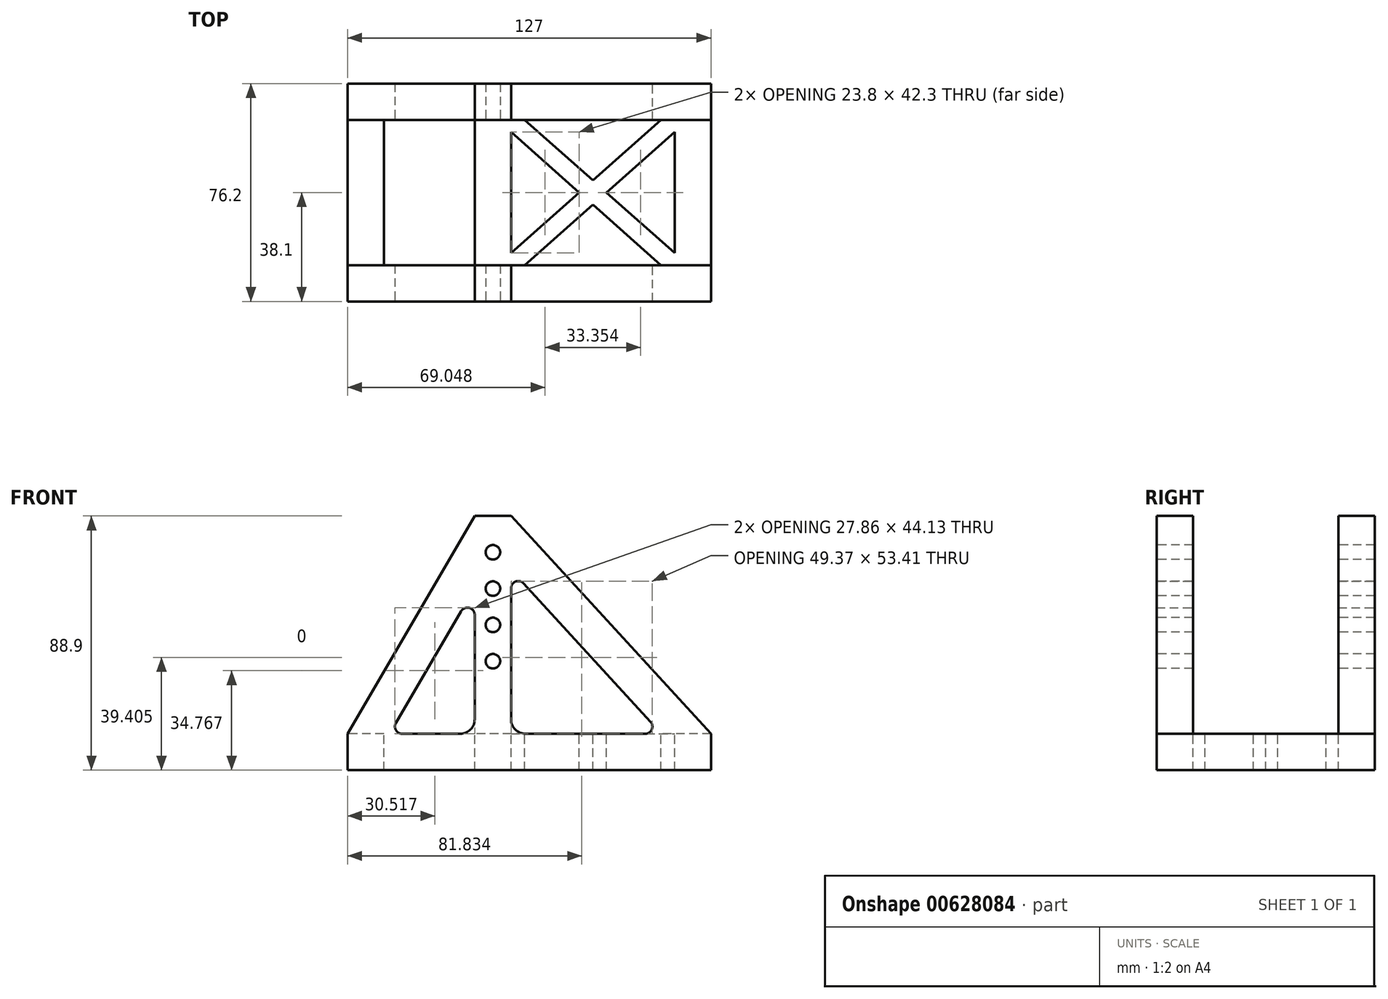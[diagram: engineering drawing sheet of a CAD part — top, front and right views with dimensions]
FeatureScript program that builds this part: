
annotation { "Feature Type Name" : "Feature", "Feature Type Description" : "" }
export const myFeature = defineFeature(function(context is Context, id is Id, definition is map)
    precondition{}
    {
        {
            var Q0;
            Q0=qCreatedBy(makeId("Front.planeOp"),FACE);
            var sketch = newSketch(context, id + "F0", { "sketchPlane" : qUnion([Q0])});
            skLineSegment(sketch, "E0", {"start": v(0, 0) * mm, "end": v(76.2, 0) * mm});
            skLineSegment(sketch, "E1", {"start": v(76.2, 0) * mm, "end": v(-50.8, 0) * mm});
            skLineSegment(sketch, "E2", {"start": v(-50.8, 0) * mm, "end": v(-50.8, 12.7) * mm});
            skLineSegment(sketch, "E3", {"start": v(-36.1, 12.7) * mm, "end": v(-6.35, 12.7) * mm});
            skLineSegment(sketch, "E4", {"start": v(76.2, 12.7) * mm, "end": v(76.2, 0) * mm});
            skLineSegment(sketch, "E5", {"start": v(0, 0) * mm, "end": v(0, 88.9) * mm, "construction": true});
            skLineSegment(sketch, "E6.bottom", {"start": v(6.35, 88.9) * mm, "end": v(-6.35, 88.9) * mm});
            skLineSegment(sketch, "E6.top", {"start": v(6.35, 88.9) * mm, "end": v(-6.35, 88.9) * mm});
            skLineSegment(sketch, "E6.left", {"start": v(6.35, 88.9) * mm, "end": v(6.35, 88.9) * mm});
            skLineSegment(sketch, "E6.right", {"start": v(-6.35, 88.9) * mm, "end": v(-6.35, 88.9) * mm});
            skPoint(sketch, "E6.middle", {"position": v(0, 88.9) * mm});
            skLineSegment(sketch, "E7", {"start": v(-6.35, 88.9) * mm, "end": v(-50.8, 12.7) * mm});
            skLineSegment(sketch, "E8", {"start": v(6.35, 88.9) * mm, "end": v(76.2, 12.7) * mm});
            skLineSegment(sketch, "E9", {"start": v(-6.35, 63.7) * mm, "end": v(-6.35, 12.7) * mm});
            skLineSegment(sketch, "E10.trimOffspring", {"start": v(-6.35, 63.7) * mm, "end": v(-36.1, 12.7) * mm});
            skLineSegment(sketch, "E11.trimOffspring", {"start": v(6.35, 70.1) * mm, "end": v(58.97, 12.7) * mm});
            skLineSegment(sketch, "E12.trimOffspring", {"start": v(6.35, 70.1) * mm, "end": v(6.35, 12.7) * mm});
            skLineSegment(sketch, "E13.trimOffspring", {"start": v(6.35, 12.7) * mm, "end": v(58.97, 12.7) * mm});
            skPoint(sketch, "E14.orphan", {"position": v(6.35, 0) * mm});
            skPoint(sketch, "E15", {"position": v(0, 76.2) * mm});
            skPoint(sketch, "E16", {"position": v(0, 63.5) * mm});
            skPoint(sketch, "E17", {"position": v(0, 50.8) * mm});
            skPoint(sketch, "E18", {"position": v(0, 38.1) * mm});
            skCircle(sketch, "E19", {"center": v(0, 38.1) * mm, "radius": 2.25 * mm});
            skCircle(sketch, "E20", {"center": v(0, 50.8) * mm, "radius": 2.25 * mm});
            skCircle(sketch, "E21", {"center": v(0, 63.5) * mm, "radius": 2.25 * mm});
            skCircle(sketch, "E22", {"center": v(0, 76.2) * mm, "radius": 2.25 * mm});
            skSolve(sketch);
        }
        {
            var Q0;
            Q0 = qSketchRegion(id + "F0", true);
            extrude(context, id + "F1", {"entities" : qUnion([Q0]), "depth" : 76.2 * mm, "offsetDistance" : 25.4 * mm});
        }
        {
            var Q0;
            Q0=makeQuery(id+"F1.opExtrude","SWEPT_FACE",FACE,{"disambiguationData":[OSD([sQuery(id+"F0.wireOp",EDGE,"E2")])]});
            var sketch = newSketch(context, id + "F2", { "sketchPlane" : qUnion([Q0])});
            skLineSegment(sketch, "E23.bottom", {"start": v(0, 0) * mm, "end": v(76.2, 0) * mm});
            skLineSegment(sketch, "E23.top", {"start": v(0, 12.7) * mm, "end": v(76.2, 12.7) * mm});
            skLineSegment(sketch, "E23.left", {"start": v(0, 0) * mm, "end": v(0, 12.7) * mm});
            skLineSegment(sketch, "E23.right", {"start": v(76.2, 0) * mm, "end": v(76.2, 12.7) * mm});
            skLineSegment(sketch, "E24", {"start": v(76.2, 12.7) * mm, "end": v(63.5, 12.7) * mm});
            skLineSegment(sketch, "E25", {"start": v(12.7, 12.7) * mm, "end": v(12.7, 88.9) * mm});
            skLineSegment(sketch, "E26", {"start": v(12.7, 88.9) * mm, "end": v(63.5, 88.9) * mm});
            skLineSegment(sketch, "E27", {"start": v(63.5, 88.9) * mm, "end": v(63.5, 12.7) * mm});
            skSolve(sketch);
        }
        {
            var Q0;
            {var subQ2=sQuery(id+"F2.wireOp",EDGE,"E25");Q0=makeQuery(id+"F2.imprint","IMPRINT",FACE,{"disambiguationData":[TD([[makeQuery(id+"F2.imprint","IMPRINT",EDGE,{"derivedFrom":subQ2}),-1.0]])]});}
            extrude(context, id + "F3", {"entities" : qUnion([Q0]), "operationType" : NewBodyOperationType.REMOVE, "oppositeDirection" : true, "depth" : 254 * mm, "offsetDistance" : 25.4 * mm});
        }
        {
            var Q0;
            Q0=makeQuery(id+"F3.boolean.opBoolean","MERGE",FACE,{"derivedFrom":[makeQuery(id+"F1.opExtrude","SWEPT_FACE",FACE,{"disambiguationData":[OSD([sQuery(id+"F0.wireOp",EDGE,"E3")])]}),makeQuery(id+"F1.opExtrude","SWEPT_FACE",FACE,{"disambiguationData":[OSD([sQuery(id+"F0.wireOp",EDGE,"E13.trimOffspring")])]}),makeQuery(id+"F3.opExtrude","SWEPT_FACE",FACE,{"disambiguationData":[OSD([sQuery(id+"F2.wireOp",EDGE,"E23.top")])]})]});
            var sketch = newSketch(context, id + "F4", { "sketchPlane" : qUnion([Q0])});
            skLineSegment(sketch, "E28.bottom", {"start": v(-50.8, -12.7) * mm, "end": v(76.2, -12.7) * mm});
            skLineSegment(sketch, "E28.top", {"start": v(-50.8, -63.5) * mm, "end": v(76.2, -63.5) * mm});
            skLineSegment(sketch, "E28.left", {"start": v(-50.8, -12.7) * mm, "end": v(-50.8, -63.5) * mm});
            skLineSegment(sketch, "E28.right", {"start": v(76.2, -12.7) * mm, "end": v(76.2, -63.5) * mm});
            skLineSegment(sketch, "E29.0", {"start": v(63.5, -12.7) * mm, "end": v(63.5, -63.5) * mm});
            skLineSegment(sketch, "E30.0", {"start": v(-38.1, -12.7) * mm, "end": v(-38.1, -63.5) * mm});
            skLineSegment(sketch, "E31", {"start": v(6.35, -12.7) * mm, "end": v(6.35, -63.5) * mm});
            skLineSegment(sketch, "E32", {"start": v(6.35, -63.5) * mm, "end": v(-6.35, -63.5) * mm});
            skLineSegment(sketch, "E33", {"start": v(-6.35, -63.5) * mm, "end": v(-6.35, -12.7) * mm});
            skLineSegment(sketch, "E34.0", {"start": v(11.13, -63.5) * mm, "end": v(34.92, -42.35) * mm});
            skLineSegment(sketch, "E35.0", {"start": v(6.35, -59.25) * mm, "end": v(30.15, -38.1) * mm});
            skLineSegment(sketch, "E36.0", {"start": v(11.13, -12.7) * mm, "end": v(34.92, -33.85) * mm});
            skLineSegment(sketch, "E37.0", {"start": v(6.35, -16.95) * mm, "end": v(30.15, -38.1) * mm});
            skLineSegment(sketch, "E38.trimOffspring", {"start": v(34.92, -42.35) * mm, "end": v(58.72, -63.5) * mm});
            skLineSegment(sketch, "E39.trimOffspring", {"start": v(39.7, -38.1) * mm, "end": v(63.5, -16.95) * mm});
            skLineSegment(sketch, "E40.trimOffspring", {"start": v(39.7, -38.1) * mm, "end": v(63.5, -59.25) * mm});
            skLineSegment(sketch, "E41.trimOffspring", {"start": v(34.92, -33.85) * mm, "end": v(58.72, -12.7) * mm});
            skSolve(sketch);
        }
        {
            var Q0;
            {var subQ0=sQuery(id+"F4.wireOp",EDGE,"E36.0");Q0=makeQuery(id+"F4.imprint","IMPRINT",FACE,{"disambiguationData":[TD([[makeQuery(id+"F4.imprint","IMPRINT",EDGE,{"derivedFrom":subQ0}),1.0]])]});}
            var Q1;
            {var subQ0=sQuery(id+"F4.wireOp",EDGE,"E34.0");Q1=makeQuery(id+"F4.imprint","IMPRINT",FACE,{"disambiguationData":[TD([[makeQuery(id+"F4.imprint","IMPRINT",EDGE,{"derivedFrom":subQ0}),-1.0]])]});}
            var Q2;
            {var subQ32=sQuery(id+"F4.wireOp",EDGE,"E30.0");Q2=makeQuery(id+"F4.imprint","IMPRINT",FACE,{"disambiguationData":[TD([[makeQuery(id+"F4.imprint","IMPRINT",EDGE,{"derivedFrom":subQ32}),1.0]])]});}
            var Q3;
            {var subQ0=sQuery(id+"F4.wireOp",EDGE,"E35.0");Q3=makeQuery(id+"F4.imprint","IMPRINT",FACE,{"disambiguationData":[TD([[makeQuery(id+"F4.imprint","IMPRINT",EDGE,{"derivedFrom":subQ0}),1.0]])]});}
            var Q4;
            {var subQ0=sQuery(id+"F4.wireOp",EDGE,"E39.trimOffspring");Q4=makeQuery(id+"F4.imprint","IMPRINT",FACE,{"disambiguationData":[TD([[makeQuery(id+"F4.imprint","IMPRINT",EDGE,{"derivedFrom":subQ0}),-1.0]])]});}
            extrude(context, id + "F5", {"entities" : qUnion([Q0, Q1, Q2, Q3, Q4]), "operationType" : NewBodyOperationType.REMOVE, "oppositeDirection" : true, "depth" : 25.4 * mm, "offsetDistance" : 25.4 * mm});
        }
        {
            var Q0;
            {var subQ1=sQuery(id+"F0.wireOp",EDGE,"E9");var subQ2=sQuery(id+"F0.wireOp",EDGE,"E3");Q0=makeQuery(id+"F3.boolean.opBoolean","SPLIT",EDGE,{"disambiguationData":[TD([makeQuery(id+"F3.opExtrude","SWEPT_FACE",FACE,{"disambiguationData":[OSD([sQuery(id+"F2.wireOp",EDGE,"E27")])]})])],"derivedFrom":makeQuery(id+"F1.opExtrude","SWEPT_EDGE",EDGE,{"disambiguationData":[OSD([subQ2,subQ1])]})});}
            var Q1;
            {var subQ0=sQuery(id+"F0.wireOp",EDGE,"E13.trimOffspring");var subQ1=sQuery(id+"F0.wireOp",EDGE,"E12.trimOffspring");Q1=makeQuery(id+"F3.boolean.opBoolean","SPLIT",EDGE,{"disambiguationData":[TD([makeQuery(id+"F3.opExtrude","SWEPT_FACE",FACE,{"disambiguationData":[OSD([sQuery(id+"F2.wireOp",EDGE,"E27")])]})])],"derivedFrom":makeQuery(id+"F1.opExtrude","SWEPT_EDGE",EDGE,{"disambiguationData":[OSD([subQ1,subQ0])]})});}
            var Q2;
            {var subQ1=sQuery(id+"F0.wireOp",EDGE,"E9");var subQ2=sQuery(id+"F0.wireOp",EDGE,"E3");Q2=makeQuery(id+"F3.boolean.opBoolean","SPLIT",EDGE,{"disambiguationData":[TD([makeQuery(id+"F3.opExtrude","SWEPT_FACE",FACE,{"disambiguationData":[OSD([sQuery(id+"F2.wireOp",EDGE,"E25")])]})])],"derivedFrom":makeQuery(id+"F1.opExtrude","SWEPT_EDGE",EDGE,{"disambiguationData":[OSD([subQ2,subQ1])]})});}
            var Q3;
            {var subQ0=sQuery(id+"F0.wireOp",EDGE,"E13.trimOffspring");var subQ1=sQuery(id+"F0.wireOp",EDGE,"E12.trimOffspring");Q3=makeQuery(id+"F3.boolean.opBoolean","SPLIT",EDGE,{"disambiguationData":[TD([makeQuery(id+"F3.opExtrude","SWEPT_FACE",FACE,{"disambiguationData":[OSD([sQuery(id+"F2.wireOp",EDGE,"E25")])]})])],"derivedFrom":makeQuery(id+"F1.opExtrude","SWEPT_EDGE",EDGE,{"disambiguationData":[OSD([subQ1,subQ0])]})});}
            fillet(context, id + "F6", {"entities" : qUnion([Q0, Q1, Q2, Q3]), "radius" : 5.08 * mm, "tangentPropagation" : true, "allowEdgeOverflow" : false});
        }
        {
            var Q0;
            {var subQ0=sQuery(id+"F0.wireOp",EDGE,"E10.trimOffspring");var subQ1=sQuery(id+"F0.wireOp",EDGE,"E9");Q0=makeQuery(id+"F3.boolean.opBoolean","SPLIT",EDGE,{"disambiguationData":[TD([makeQuery(id+"F3.opExtrude","SWEPT_FACE",FACE,{"disambiguationData":[OSD([sQuery(id+"F2.wireOp",EDGE,"E27")])]})])],"derivedFrom":makeQuery(id+"F1.opExtrude","SWEPT_EDGE",EDGE,{"disambiguationData":[OSD([subQ1,subQ0])]})});}
            var Q1;
            {var subQ0=sQuery(id+"F0.wireOp",EDGE,"E13.trimOffspring");var subQ1=sQuery(id+"F0.wireOp",EDGE,"E11.trimOffspring");Q1=makeQuery(id+"F3.boolean.opBoolean","SPLIT",EDGE,{"disambiguationData":[TD([makeQuery(id+"F3.opExtrude","SWEPT_FACE",FACE,{"disambiguationData":[OSD([sQuery(id+"F2.wireOp",EDGE,"E27")])]})])],"derivedFrom":makeQuery(id+"F1.opExtrude","SWEPT_EDGE",EDGE,{"disambiguationData":[OSD([subQ1,subQ0])]})});}
            var Q2;
            {var subQ0=sQuery(id+"F0.wireOp",EDGE,"E12.trimOffspring");var subQ1=sQuery(id+"F0.wireOp",EDGE,"E11.trimOffspring");Q2=makeQuery(id+"F3.boolean.opBoolean","SPLIT",EDGE,{"disambiguationData":[TD([makeQuery(id+"F3.opExtrude","SWEPT_FACE",FACE,{"disambiguationData":[OSD([sQuery(id+"F2.wireOp",EDGE,"E27")])]})])],"derivedFrom":makeQuery(id+"F1.opExtrude","SWEPT_EDGE",EDGE,{"disambiguationData":[OSD([subQ1,subQ0])]})});}
            var Q3;
            {var subQ0=sQuery(id+"F0.wireOp",EDGE,"E12.trimOffspring");var subQ1=sQuery(id+"F0.wireOp",EDGE,"E11.trimOffspring");Q3=makeQuery(id+"F3.boolean.opBoolean","SPLIT",EDGE,{"disambiguationData":[TD([makeQuery(id+"F3.opExtrude","SWEPT_FACE",FACE,{"disambiguationData":[OSD([sQuery(id+"F2.wireOp",EDGE,"E25")])]})])],"derivedFrom":makeQuery(id+"F1.opExtrude","SWEPT_EDGE",EDGE,{"disambiguationData":[OSD([subQ1,subQ0])]})});}
            var Q4;
            {var subQ0=sQuery(id+"F0.wireOp",EDGE,"E10.trimOffspring");var subQ1=sQuery(id+"F0.wireOp",EDGE,"E9");Q4=makeQuery(id+"F3.boolean.opBoolean","SPLIT",EDGE,{"disambiguationData":[TD([makeQuery(id+"F3.opExtrude","SWEPT_FACE",FACE,{"disambiguationData":[OSD([sQuery(id+"F2.wireOp",EDGE,"E25")])]})])],"derivedFrom":makeQuery(id+"F1.opExtrude","SWEPT_EDGE",EDGE,{"disambiguationData":[OSD([subQ1,subQ0])]})});}
            var Q5;
            {var subQ0=sQuery(id+"F0.wireOp",EDGE,"E13.trimOffspring");var subQ2=sQuery(id+"F0.wireOp",EDGE,"E11.trimOffspring");Q5=makeQuery(id+"F3.boolean.opBoolean","SPLIT",EDGE,{"disambiguationData":[TD([makeQuery(id+"F3.opExtrude","SWEPT_FACE",FACE,{"disambiguationData":[OSD([sQuery(id+"F2.wireOp",EDGE,"E25")])]})])],"derivedFrom":makeQuery(id+"F1.opExtrude","SWEPT_EDGE",EDGE,{"disambiguationData":[OSD([subQ2,subQ0])]})});}
            var Q6;
            {var subQ1=sQuery(id+"F0.wireOp",EDGE,"E10.trimOffspring");var subQ2=sQuery(id+"F0.wireOp",EDGE,"E3");Q6=makeQuery(id+"F3.boolean.opBoolean","SPLIT",EDGE,{"disambiguationData":[TD([makeQuery(id+"F3.opExtrude","SWEPT_FACE",FACE,{"disambiguationData":[OSD([sQuery(id+"F2.wireOp",EDGE,"E25")])]})])],"derivedFrom":makeQuery(id+"F1.opExtrude","SWEPT_EDGE",EDGE,{"disambiguationData":[OSD([subQ2,subQ1])]})});}
            fillet(context, id + "F7", {"entities" : qUnion([Q0, Q1, Q2, Q3, Q4, Q5, Q6]), "radius" : 2.54 * mm, "tangentPropagation" : true, "allowEdgeOverflow" : false});
        }
        {
            var Q0;
            {var subQ1=sQuery(id+"F0.wireOp",EDGE,"E10.trimOffspring");var subQ2=sQuery(id+"F0.wireOp",EDGE,"E3");Q0=makeQuery(id+"F3.boolean.opBoolean","SPLIT",EDGE,{"disambiguationData":[TD([makeQuery(id+"F3.opExtrude","SWEPT_FACE",FACE,{"disambiguationData":[OSD([sQuery(id+"F2.wireOp",EDGE,"E27")])]})])],"derivedFrom":makeQuery(id+"F1.opExtrude","SWEPT_EDGE",EDGE,{"disambiguationData":[OSD([subQ2,subQ1])]})});}
            fillet(context, id + "F8", {"entities" : qUnion([Q0]), "radius" : 2.54 * mm, "tangentPropagation" : true, "allowEdgeOverflow" : false});
        }
        {
            var Q0;
            Q0=makeQuery(id+"F1.opExtrude","CAP_FACE",FACE,{"disambiguationData":[OSD([sQuery(id+"F0.wireOp",EDGE,"E1"),sQuery(id+"F0.wireOp",EDGE,"E2"),sQuery(id+"F0.wireOp",EDGE,"E3"),sQuery(id+"F0.wireOp",EDGE,"E4"),sQuery(id+"F0.wireOp",EDGE,"E6.top"),sQuery(id+"F0.wireOp",EDGE,"E7"),sQuery(id+"F0.wireOp",EDGE,"E8"),sQuery(id+"F0.wireOp",EDGE,"E9"),sQuery(id+"F0.wireOp",EDGE,"E10.trimOffspring"),sQuery(id+"F0.wireOp",EDGE,"E11.trimOffspring"),sQuery(id+"F0.wireOp",EDGE,"E12.trimOffspring"),sQuery(id+"F0.wireOp",EDGE,"E13.trimOffspring"),sQuery(id+"F0.wireOp",EDGE,"E19"),sQuery(id+"F0.wireOp",EDGE,"E20"),sQuery(id+"F0.wireOp",EDGE,"E21"),sQuery(id+"F0.wireOp",EDGE,"E22")])],"isStart":false});
            var sketch = newSketch(context, id + "F9", { "sketchPlane" : qUnion([Q0])});
            skCircle(sketch, "E42", {"center": v(0, 76.2) * mm, "radius": 2.54 * mm});
            skCircle(sketch, "E43", {"center": v(0, 63.5) * mm, "radius": 2.54 * mm});
            skCircle(sketch, "E44", {"center": v(0, 50.8) * mm, "radius": 2.54 * mm});
            skCircle(sketch, "E45", {"center": v(0, 38.1) * mm, "radius": 2.54 * mm});
            skSolve(sketch);
        }
        {
            var Q0;
            Q0 = qSketchRegion(id + "F9", true);
            extrude(context, id + "F10", {"entities" : qUnion([Q0]), "operationType" : NewBodyOperationType.REMOVE, "oppositeDirection" : true, "depth" : 254 * mm, "offsetDistance" : 25.4 * mm});
        }
    });
